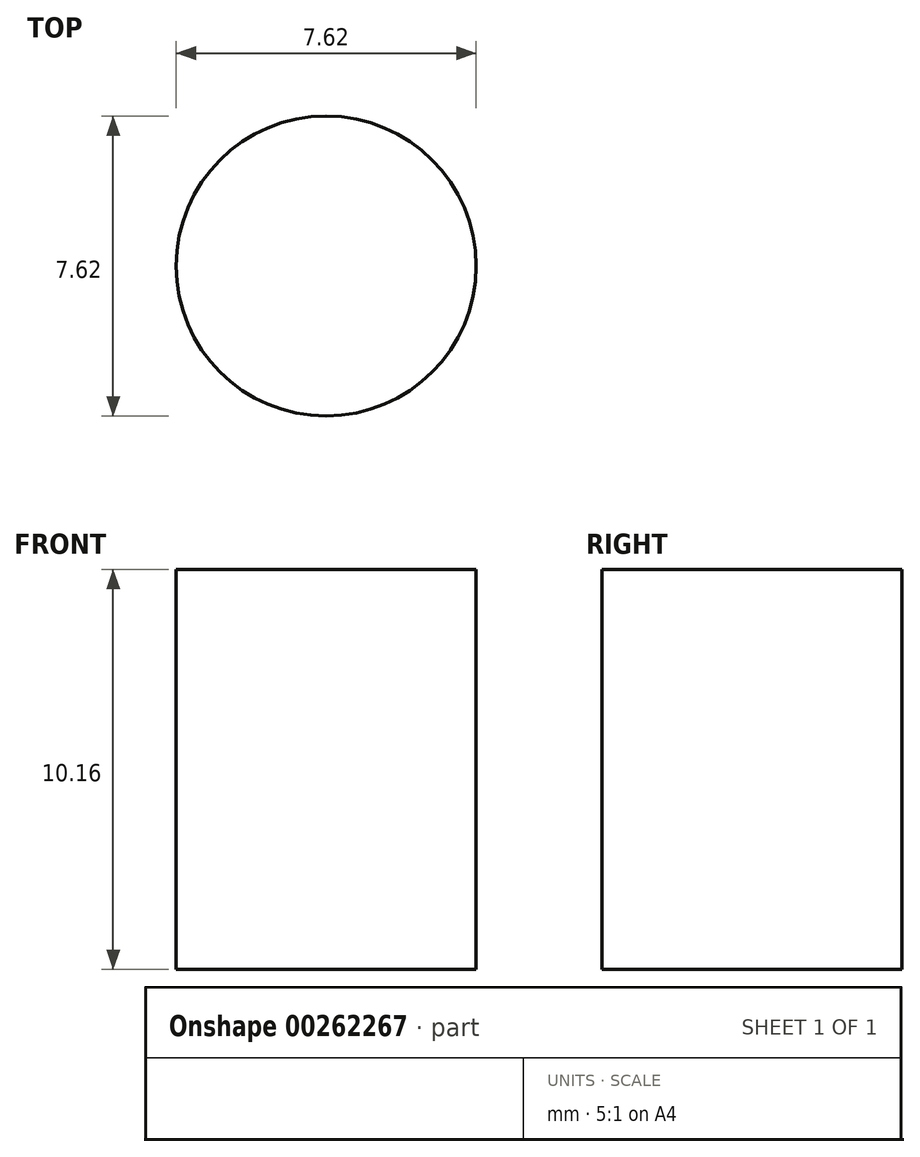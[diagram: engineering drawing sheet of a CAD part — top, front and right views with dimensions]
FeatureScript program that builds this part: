
annotation { "Feature Type Name" : "Feature", "Feature Type Description" : "" }
export const myFeature = defineFeature(function(context is Context, id is Id, definition is map)
    precondition{}
    {
        {
            var Q0;
            Q0=qCreatedBy(makeId("Top.planeOp"),FACE);
            var sketch = newSketch(context, id + "F0", { "sketchPlane" : qUnion([Q0])});
            skCircle(sketch, "E0", {"center": v(0, 0) * mm, "radius": 3.81 * mm});
            skSolve(sketch);
        }
        {
            var Q0;
            Q0 = qSketchRegion(id + "F0", true);
            extrude(context, id + "F1", {"entities" : qUnion([Q0]), "depth" : 10.16 * mm});
        }
    });
